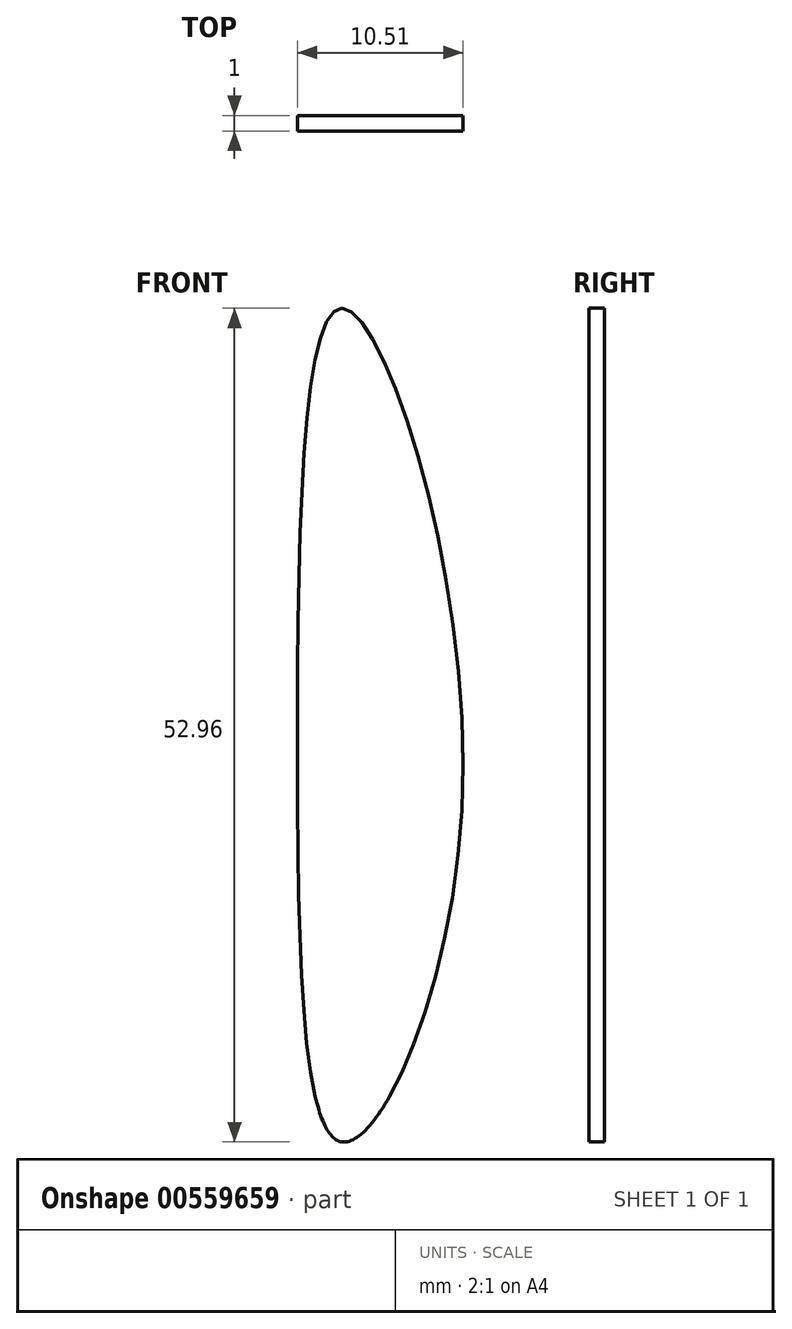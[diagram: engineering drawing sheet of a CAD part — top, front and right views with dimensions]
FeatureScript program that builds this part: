
annotation { "Feature Type Name" : "Feature", "Feature Type Description" : "" }
export const myFeature = defineFeature(function(context is Context, id is Id, definition is map)
    precondition{}
    {
        {
            var Q0;
            Q0=qCreatedBy(makeId("Front.planeOp"),FACE);
            var sketch = newSketch(context, id + "F0", { "sketchPlane" : qUnion([Q0])});
            skLineSegment(sketch, "E0", {"start": v(0, 0) * mm, "end": v(0, 52.95) * mm});
            skFitSpline(sketch, "E1", {"points": [v(0, 52.95) * mm, v(7.65, 22.1) * mm, v(0, 0) * mm, v(-2.83, 24.93) * mm, v(0, 52.95) * mm]});
            skLineSegment(sketch, "E2", {"start": v(-1.7, 2.9) * mm, "end": v(3.02, 2.9) * mm});
            skSolve(sketch);
        }
        {
            var Q0;
            Q0 = qSketchRegion(id + "F0", true);
            extrude(context, id + "F1", {"entities" : qUnion([Q0]), "depth" : 1 * mm, "offsetDistance" : 25 * mm});
        }
    });
